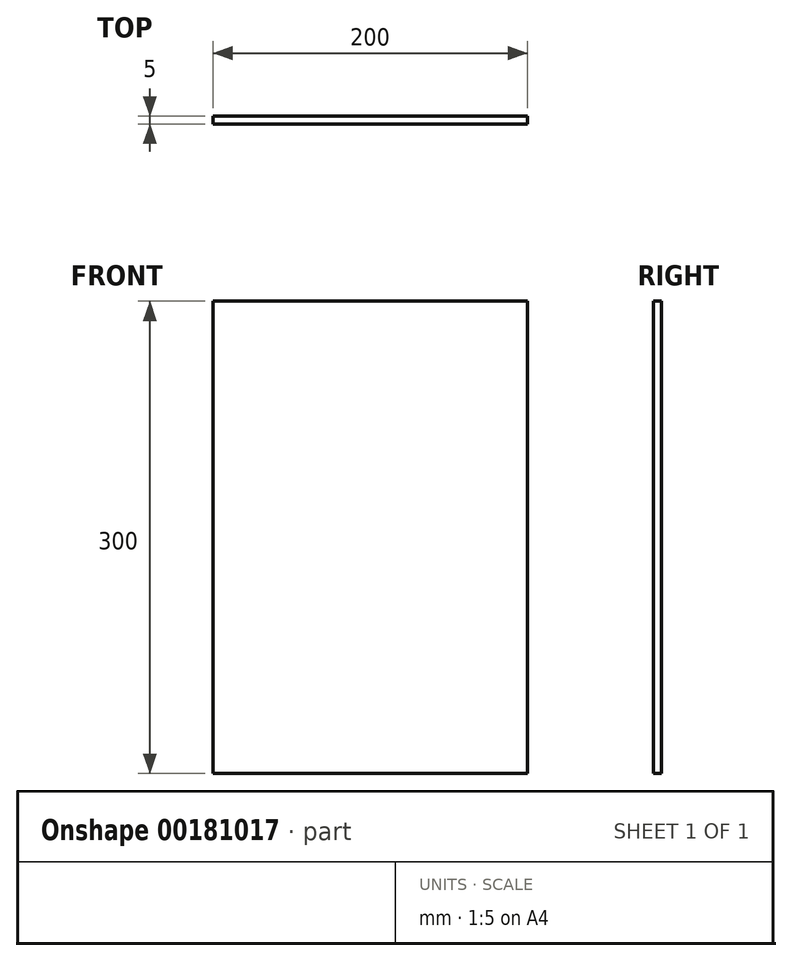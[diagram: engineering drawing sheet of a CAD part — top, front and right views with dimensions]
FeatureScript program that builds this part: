
annotation { "Feature Type Name" : "Feature", "Feature Type Description" : "" }
export const myFeature = defineFeature(function(context is Context, id is Id, definition is map)
    precondition{}
    {
        {
            var Q0;
            Q0=qCreatedBy(makeId("Front.planeOp"),FACE);
            var sketch = newSketch(context, id + "F0", { "sketchPlane" : qUnion([Q0])});
            skLineSegment(sketch, "E0.bottom", {"start": v(0, 0) * mm, "end": v(200, 0) * mm});
            skLineSegment(sketch, "E0.top", {"start": v(0, 300) * mm, "end": v(200, 300) * mm});
            skLineSegment(sketch, "E0.left", {"start": v(0, 0) * mm, "end": v(0, 300) * mm});
            skLineSegment(sketch, "E0.right", {"start": v(200, 0) * mm, "end": v(200, 300) * mm});
            skPoint(sketch, "E1.centerSnap0", {"position": v(0, 150) * mm});
            skSolve(sketch);
        }
        {
            var Q0;
            Q0=qSketchRegion(id+"F0",true);
            extrude(context, id + "F1", {"entities" : qUnion([Q0]), "depth" : 5 * mm});
        }
    });
